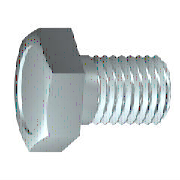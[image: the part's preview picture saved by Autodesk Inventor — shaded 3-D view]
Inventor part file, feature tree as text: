
AUTODESK INVENTOR PART (.ipt)
format: ipt  version: 2021 (Build 250183000, 183)  size: 204,800 bytes
history: native  units: mm (DEFAULTED — no unit token found)
features: sketch x4, extrude x2, chamfer x1, plane x1
ambient origin geometry x7: Origin, YZ Plane, XY Plane, X Axis, Y Axis, Z Axis, Center Point
bodies: Solid1 (feature_tree), Body (feature_tree)
feature tree (8):
  extrude  "Head"  Depth=20.0mm
  extrude  "Indent1"  Depth=13.0mm
  chamfer  "Chamfer1"  Angle=30.0deg  [1 undecoded]
  plane  "Work Plane1"
  sketch  "Sketch1"  dims[d0=8.0mm d1=20.0mm]
  sketch  "Sketch2"  dims[d5=90.0deg d2=13.0mm]
  sketch  "Sketch4"  dims[d4=0.0mm d6=30.0deg d7=30.0deg d13=90.0deg d8=17.5mm d9=0.0mm d11=0.4mm d12=9.75mm d14=1.3mm d15=0.0mm d16=13.0mm d17=13.0mm d18=15.011107mm d20=0.0mm d33=0.0mm d34=0.0mm]
  sketch  "Sketch3"  dims[d3=6.5mm]
note: 1 required parameter value undecoded (feature->parameter linkage not recoverable at this tier; creation-order binding heuristic only, values carry confidence <= 0.55)
